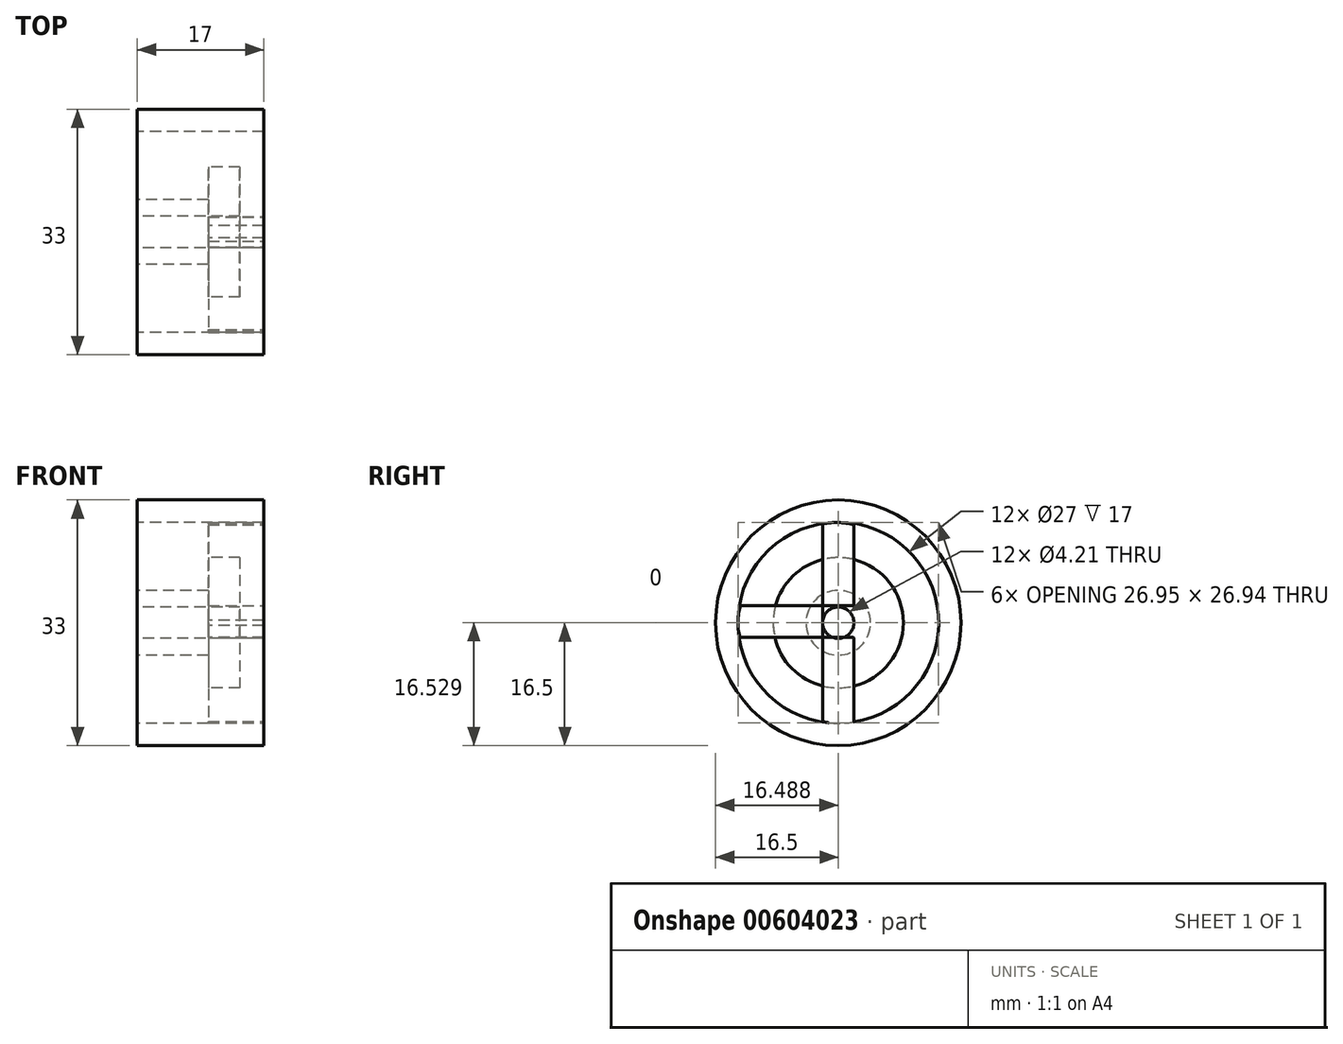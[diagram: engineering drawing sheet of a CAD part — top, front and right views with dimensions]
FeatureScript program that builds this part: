
annotation { "Feature Type Name" : "Feature", "Feature Type Description" : "" }
export const myFeature = defineFeature(function(context is Context, id is Id, definition is map)
    precondition{}
    {
        {
            var Q0;
            Q0=qCreatedBy(makeId("Front.planeOp"),FACE);
            var sketch = newSketch(context, id + "F0", { "sketchPlane" : qUnion([Q0])});
            skLineSegment(sketch, "E0.bottom", {"start": v(0, 0) * mm, "end": v(17, 0) * mm});
            skLineSegment(sketch, "E0.top", {"start": v(0, 16.5) * mm, "end": v(17, 16.5) * mm});
            skLineSegment(sketch, "E0.left", {"start": v(0, 0) * mm, "end": v(0, 4.35) * mm});
            skLineSegment(sketch, "E0.right", {"start": v(17, 13.5) * mm, "end": v(17, 16.5) * mm});
            skLineSegment(sketch, "E1", {"start": v(0, 13.5) * mm, "end": v(17, 13.5) * mm});
            skLineSegment(sketch, "E2", {"start": v(0, 4.35) * mm, "end": v(9.57, 4.35) * mm});
            skLineSegment(sketch, "E3", {"start": v(9.57, 4.35) * mm, "end": v(9.57, 8.75) * mm});
            skLineSegment(sketch, "E4", {"start": v(9.57, 8.75) * mm, "end": v(13.77, 8.75) * mm});
            skLineSegment(sketch, "E5", {"start": v(13.77, 8.75) * mm, "end": v(13.77, 0) * mm});
            skLineSegment(sketch, "E6.trimOffspring", {"start": v(0, 13.5) * mm, "end": v(0, 16.5) * mm});
            skLineSegment(sketch, "E7", {"start": v(-49.72, 0) * mm, "end": v(15.27, 0) * mm, "construction": true});
            skSolve(sketch);
        }
        {
            var Q0;
            {var subQ0=sQuery(id+"F0.wireOp",EDGE,"E0.left");Q0=makeQuery(id+"F0.imprint","IMPRINT",FACE,{"disambiguationData":[TD([[makeQuery(id+"F0.imprint","IMPRINT",EDGE,{"derivedFrom":subQ0}),-1.0]])]});}
            var Q1;
            Q1=makeQuery(id+"F0.imprint","IMPRINT",FACE,{"disambiguationData":[TD([[makeQuery(id+"F0.imprint","IMPRINT",EDGE,{"derivedFrom":sQuery(id+"F0.wireOp",EDGE,"E0.top")}),-1.0]])]});
            var Q2;
            Q2=sQuery(id+"F0.wireOp",EDGE,"E7");
            revolve(context, id + "F1", {"entities" : qUnion([Q0, Q1]), "axis" : qUnion([Q2]), "revolveType" : RevolveType.FULL});
        }
        {
            var Q0;
            Q0=qCreatedBy(makeId("Right.planeOp"),FACE);
            var sketch = newSketch(context, id + "F2", { "sketchPlane" : qUnion([Q0])});
            skCircle(sketch, "E8", {"center": v(0, 0) * mm, "radius": 2.1 * mm});
            skSolve(sketch);
        }
        {
            var Q0;
            Q0=makeQuery(id+"F2.imprint","IMPRINT",FACE,{"disambiguationData":[TD([[makeQuery(id+"F2.imprint","IMPRINT",EDGE,{"derivedFrom":sQuery(id+"F2.wireOp",EDGE,"E8")}),1.0]])]});
            extrude(context, id + "F3", {"entities" : qUnion([Q0]), "operationType" : NewBodyOperationType.REMOVE, "endBound" : BoundingType.THROUGH_ALL, "depth" : 25 * mm, "offsetDistance" : 25 * mm});
        }
        {
            var Q0;
            Q0=makeQuery(id+"F1.opRevolve","SWEPT_FACE",FACE,{"disambiguationData":[OSD([sQuery(id+"F0.wireOp",EDGE,"E0.right")])]});
            var sketch = newSketch(context, id + "F4", { "sketchPlane" : qUnion([Q0])});
            skLineSegment(sketch, "E9", {"start": v(2.08, 3.82) * mm, "end": v(2.08, 13.15) * mm});
            skLineSegment(sketch, "E10", {"start": v(-2.08, 3.82) * mm, "end": v(-2.08, 13.28) * mm});
            skLineSegment(sketch, "E11", {"start": v(-2.08, 3.82) * mm, "end": v(-2.08, -13.28) * mm});
            skLineSegment(sketch, "E12", {"start": v(2.08, 3.82) * mm, "end": v(2.08, -13.34) * mm});
            skLineSegment(sketch, "E13", {"start": v(2.08, 2.32) * mm, "end": v(-13.12, 2.32) * mm});
            skLineSegment(sketch, "E14", {"start": v(-13.12, 2.32) * mm, "end": v(13.2, 2.32) * mm});
            skLineSegment(sketch, "E15", {"start": v(-3.9, -1.94) * mm, "end": v(13.32, -1.94) * mm});
            skLineSegment(sketch, "E16", {"start": v(13.32, -1.94) * mm, "end": v(-13.24, -1.94) * mm});
            skLineSegment(sketch, "E17", {"start": v(2.02, -1.94) * mm, "end": v(2.08, -1.99) * mm});
            skLineSegment(sketch, "E18", {"start": v(-2.01, -1.94) * mm, "end": v(-2.08, -2) * mm});
            skLineSegment(sketch, "E19", {"start": v(-2.08, -2) * mm, "end": v(-2.01, -1.94) * mm});
            skLineSegment(sketch, "E20", {"start": v(0, 0) * mm, "end": v(0.08, 0.08) * mm});
            skLineSegment(sketch, "E21", {"start": v(2.41, 2.32) * mm, "end": v(2.08, 2) * mm});
            skLineSegment(sketch, "E22.trimOffspring", {"start": v(2.08, 2) * mm, "end": v(2.41, 2.32) * mm});
            skLineSegment(sketch, "E23.trimOffspring", {"start": v(0.08, 0.08) * mm, "end": v(0, 0) * mm});
            skArc(sketch, "E24", {"start": v(13.32, -1.94) * mm, "mid": v(13.4, 0.2) * mm, "end": v(13.2, 2.32) * mm});
            skArc(sketch, "E25", {"start": v(-13.12, 2.32) * mm, "mid": v(-13.48, 0.2) * mm, "end": v(-13.24, -1.94) * mm});
            skArc(sketch, "E26", {"start": v(2.08, 13.15) * mm, "mid": v(0, 13.47) * mm, "end": v(-2.08, 13.28) * mm});
            skArc(sketch, "E27", {"start": v(-2.08, -13.28) * mm, "mid": v(0, -13.54) * mm, "end": v(2.08, -13.34) * mm});
            skSolve(sketch);
        }
        {
            var Q0;
            {var subQ5=sQuery(id+"F4.wireOp",EDGE,"E9");Q0=makeQuery(id+"F4.imprint","IMPRINT",FACE,{"disambiguationData":[TD([[makeQuery(id+"F4.imprint","IMPRINT",EDGE,{"derivedFrom":subQ5}),1.0]])]});}
            var Q1;
            {var subQ0=sQuery(id+"F4.wireOp",EDGE,"E25");Q1=makeQuery(id+"F4.imprint","IMPRINT",FACE,{"disambiguationData":[TD([[makeQuery(id+"F4.imprint","IMPRINT",EDGE,{"derivedFrom":subQ0}),1.0]])]});}
            var Q2;
            {var subQ5=sQuery(id+"F4.wireOp",EDGE,"E22.trimOffspring");Q2=makeQuery(id+"F4.imprint","IMPRINT",FACE,{"disambiguationData":[TD([[makeQuery(id+"F4.imprint","IMPRINT",EDGE,{"derivedFrom":subQ5}),-1.0]])]});}
            var Q3;
            {var subQ0=sQuery(id+"F4.wireOp",EDGE,"E17");Q3=makeQuery(id+"F4.imprint","IMPRINT",FACE,{"disambiguationData":[TD([[makeQuery(id+"F4.imprint","IMPRINT",EDGE,{"derivedFrom":subQ0}),-1.0]])]});}
            var Q4;
            Q4=makeQuery(id+"F1.opRevolve","SWEPT_FACE",FACE,{"disambiguationData":[OSD([sQuery(id+"F0.wireOp",EDGE,"E3")])]});
            extrude(context, id + "F5", {"entities" : qUnion([Q0, Q1, Q2, Q3]), "endBound" : BoundingType.UP_TO_SURFACE, "oppositeDirection" : true, "depth" : 25 * mm, "endBoundEntityFace" : qUnion([Q4]), "offsetDistance" : 25 * mm});
        }
        {
            var Q0;
            Q0=makeQuery(id+"F1.opRevolve","SWEPT_BODY",BODY,{"disambiguationData":[OSD([sQuery(id+"F0.wireOp",EDGE,"E0.top"),sQuery(id+"F0.wireOp",EDGE,"E0.right"),sQuery(id+"F0.wireOp",EDGE,"E1"),sQuery(id+"F0.wireOp",EDGE,"E6.trimOffspring")])]});
            var Q1;
            Q1=makeQuery(id+"F5.opExtrude","SWEPT_BODY",BODY,{"disambiguationData":[OSD([sQuery(id+"F4.wireOp",EDGE,"E12"),sQuery(id+"F4.wireOp",EDGE,"E14"),sQuery(id+"F4.wireOp",EDGE,"E16"),sQuery(id+"F4.wireOp",EDGE,"E22.trimOffspring"),sQuery(id+"F4.wireOp",EDGE,"E24")])]});
            var Q2;
            Q2=makeQuery(id+"F5.opExtrude","SWEPT_BODY",BODY,{"disambiguationData":[OSD([sQuery(id+"F0.wireOp",EDGE,"E0.right"),sQuery(id+"F0.wireOp",EDGE,"E1"),sQuery(id+"F4.wireOp",EDGE,"E11"),sQuery(id+"F4.wireOp",EDGE,"E12"),sQuery(id+"F4.wireOp",EDGE,"E16"),sQuery(id+"F4.wireOp",EDGE,"E17"),sQuery(id+"F4.wireOp",EDGE,"E19"),sQuery(id+"F4.wireOp",EDGE,"E27")])]});
            var Q3;
            Q3=makeQuery(id+"F5.opExtrude","SWEPT_BODY",BODY,{"disambiguationData":[OSD([sQuery(id+"F4.wireOp",EDGE,"E9"),sQuery(id+"F4.wireOp",EDGE,"E10"),sQuery(id+"F4.wireOp",EDGE,"E11"),sQuery(id+"F4.wireOp",EDGE,"E12"),sQuery(id+"F4.wireOp",EDGE,"E14"),sQuery(id+"F4.wireOp",EDGE,"E26")])]});
            var Q4;
            Q4=makeQuery(id+"F5.opExtrude","SWEPT_BODY",BODY,{"disambiguationData":[OSD([sQuery(id+"F4.wireOp",EDGE,"E11"),sQuery(id+"F4.wireOp",EDGE,"E14"),sQuery(id+"F4.wireOp",EDGE,"E16"),sQuery(id+"F4.wireOp",EDGE,"E25")])]});
            booleanBodies(context, id + "F6", {"operationType" : BooleanOperationType.UNION, "tools" : qUnion([Q0, Q1, Q2, Q3, Q4])});
        }
    });
